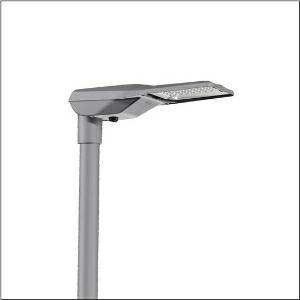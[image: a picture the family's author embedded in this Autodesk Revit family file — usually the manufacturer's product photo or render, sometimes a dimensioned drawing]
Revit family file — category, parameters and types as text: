
# Revit family: streetlight_sl_21_mini___st1_0ab_5xe2m33r08hb_9a5f
name_source: partatom
category: Lighting Fixtures
units: mm (PartAtom-declared; Revit-internal decimal feet)

## family parameters
Cut with Voids When Loaded = No
Host = Face
Light Source = No
Part Type = Normal
Room Calculation Point = No
Round Connector Dimension = Use Diameter
Shared = No

## types (1)
- --- (1 x LED, 7960 lm, 66 W, 3000K)
    Apparent Load = 66 VA
    CIE Flux Codes = 38 73 97 100 100
    Color Rendering = 70
    Color Temperature = 3000K
    Default Elevation = 1800 mm
    Description = Streetlight SL 21 mini, mast luminaire, primary light control with lens, of PMMA, primary optical cover: cover, of toughened safety glass, transparent, light distribution: ST1.0aB, light emission: direct distribution, primary light characteristic: asymmetric, installation type: side-entry, post-top, LED, High Power LED, rated luminous flux: 7.960lm, luminous efficacy: 121lm/W, light colour: 730, colour temperature: 3000K, control gear: D4i, control: flexible luminous flux parameterisation, time-dependent luminous flux control, constant luminous flux control, overheat protection, pre-setting: logarithmic dimming characteristic, mains connection: 220..240V, AC, 50/60Hz, start of lifetime: 66W, end of service life: 69W, reduction: 30W, luminaire housing, of diecast aluminium, powder-coated, SITECO metallic grey (DB 702S), corrosivity category C5 high according to DIN EN ISO 12944, please order mast flange separately, inclination adjustable: 0°, 5°, 10°, 15°, sealing non-destructively replaceable, multi-level sealing system, length: 628mm, width: 235mm, height: 110mm, mast flange for spigot size: 42mm (side-entry): 5XC10008XM4, 60/48mm (side-entry/post-top): 5XC10108XM2, 76/60mm (side-entry/post-top): 5XC10108XM1, mounting height: 4..8m, Smart Interface below, protection rating (complete): IP66, insulation class (complete): insulation class II (safety insulation), certification: CE, ENEC, ENEC+, VDE, impact resistance: IK10, permissible operating ambient temperature for outdoor applications: -40..+50°C, standard-compliant lighting for roads and squares, packaging unit: 1 piece

Light Distribution: ST1.0aB
    Height = 110 mm
    Lamp = 1 x LED
    Lamp Light Flux = 7960 lm
    Lamp Power = 66 W
    Lamp count = 1
    Length = 625 mm
    Luminous efficacy = 121 lm/W
    Manufacturer = Siteco
    ModVariant = No
    Model = 5XE2M33R08HB
    Number of Poles = 1
    OnlyDefault = Yes
    Power Factor = 1
    Product Name = Streetlight SL 21 mini | ST1.0aB
    Product group = mast luminaire | pylon top
    ProductGroupID = 6100
    Protection Class = Protection class II
    Protection Degree = IP 66
    RLX_Detail_Level = 1
    RLX_Emergency_Light_Flux = 0 lm
    RLX_Emergency_Type = 0
    RLX_Emergency_Type_DB = No
    RlxData = <blob elided: 26161 chars, md5=595ac583>
    Socket = socket
    Standby Power = 0 W
    System Light Flux = 7960 lm
    System Power = 66 W
    Type Comments = factory setting: luminous flux: 100 % | dim-lin: 254 | 670 mA
    Type Image = l_1003516.jpg
    URL = http://relux.com
    VarID = @adj_180119
    Voltage = 0 V
    Weight = 0.00 kg
    Width = 234 mm

## geometry (parser evidence)
native form markers: Blend x4, Sweep x11
no freeform markers — native parametric forms only
